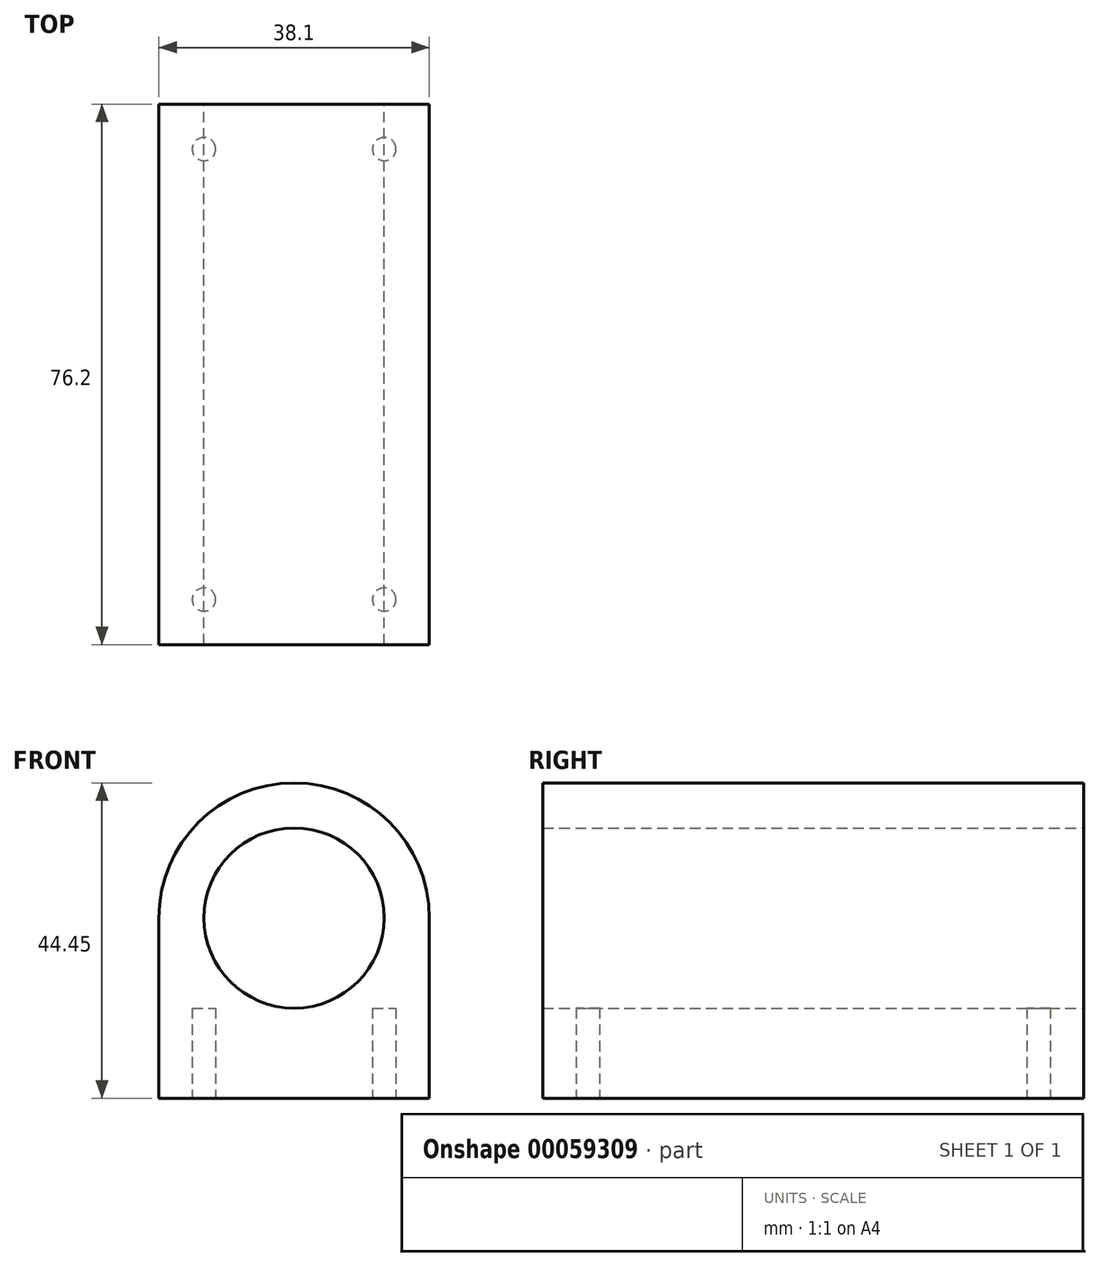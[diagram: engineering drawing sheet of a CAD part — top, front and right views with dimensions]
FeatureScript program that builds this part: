
annotation { "Feature Type Name" : "Feature", "Feature Type Description" : "" }
export const myFeature = defineFeature(function(context is Context, id is Id, definition is map)
    precondition{}
    {
        {
            var Q0;
            Q0=qCreatedBy(makeId("Front.planeOp"),FACE);
            var sketch = newSketch(context, id + "F0", { "sketchPlane" : qUnion([Q0])});
            skCircle(sketch, "E0", {"center": v(0, 0) * mm, "radius": 12.7 * mm});
            skArc(sketch, "E1", {"start": v(19.05, 0) * mm, "mid": v(0, 19.05) * mm, "end": v(-19.05, 0) * mm});
            skLineSegment(sketch, "E2", {"start": v(-19.05, 0) * mm, "end": v(-19.05, -25.4) * mm});
            skLineSegment(sketch, "E3", {"start": v(-19.05, -25.4) * mm, "end": v(19.05, -25.4) * mm});
            skLineSegment(sketch, "E4", {"start": v(19.05, 0) * mm, "end": v(19.05, -25.4) * mm});
            skSolve(sketch);
        }
        {
            var Q0;
            Q0=makeQuery(id+"F0.imprint","IMPRINT",FACE,{"disambiguationData":[TD([[makeQuery(id+"F0.imprint","IMPRINT",EDGE,{"derivedFrom":sQuery(id+"F0.wireOp",EDGE,"E0")}),-1.0]])]});
            extrude(context, id + "F1", {"entities" : qUnion([Q0]), "depth" : 76.2 * mm});
        }
        {
            var Q0;
            Q0=makeQuery(id+"F1.opExtrude","SWEPT_FACE",FACE,{"disambiguationData":[OSD([sQuery(id+"F0.wireOp",EDGE,"E3")])]});
            var sketch = newSketch(context, id + "F2", { "sketchPlane" : qUnion([Q0])});
            skCircle(sketch, "E5", {"center": v(12.7, 69.85) * mm, "radius": 1.65 * mm});
            skCircle(sketch, "E6", {"center": v(-12.7, 69.85) * mm, "radius": 1.65 * mm});
            skCircle(sketch, "E7", {"center": v(-12.7, 6.35) * mm, "radius": 1.65 * mm});
            skCircle(sketch, "E8", {"center": v(12.7, 6.35) * mm, "radius": 1.65 * mm});
            skSolve(sketch);
        }
        {
            var Q0;
            Q0=makeQuery(id+"F2.imprint","IMPRINT",FACE,{"disambiguationData":[TD([[makeQuery(id+"F2.imprint","IMPRINT",EDGE,{"derivedFrom":sQuery(id+"F2.wireOp",EDGE,"E6")}),1.0]])]});
            var Q1;
            Q1=makeQuery(id+"F2.imprint","IMPRINT",FACE,{"disambiguationData":[TD([[makeQuery(id+"F2.imprint","IMPRINT",EDGE,{"derivedFrom":sQuery(id+"F2.wireOp",EDGE,"E5")}),1.0]])]});
            var Q2;
            Q2=makeQuery(id+"F2.imprint","IMPRINT",FACE,{"disambiguationData":[TD([[makeQuery(id+"F2.imprint","IMPRINT",EDGE,{"derivedFrom":sQuery(id+"F2.wireOp",EDGE,"E7")}),1.0]])]});
            var Q3;
            Q3=makeQuery(id+"F2.imprint","IMPRINT",FACE,{"disambiguationData":[TD([[makeQuery(id+"F2.imprint","IMPRINT",EDGE,{"derivedFrom":sQuery(id+"F2.wireOp",EDGE,"E8")}),1.0]])]});
            extrude(context, id + "F3", {"entities" : qUnion([Q0, Q1, Q2, Q3]), "operationType" : NewBodyOperationType.REMOVE, "oppositeDirection" : true, "depth" : 12.7 * mm});
        }
    });
